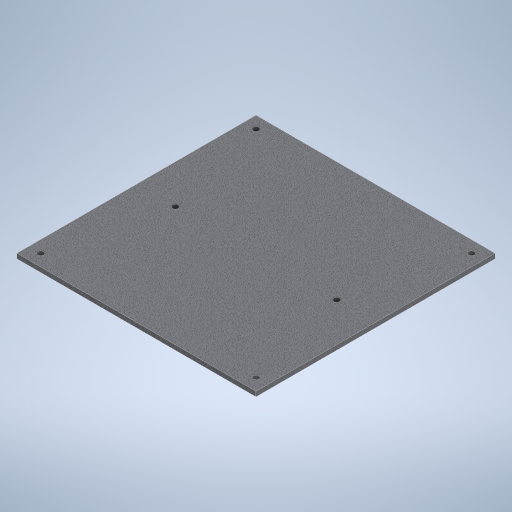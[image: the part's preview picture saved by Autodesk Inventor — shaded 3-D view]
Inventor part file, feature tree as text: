
AUTODESK INVENTOR PART (.ipt)
format: ipt  version: 2023 (Build 270158000, 158)  size: 349,184 bytes
history: native  units: mm
features: sketch x3, hole x2, other x1, extrude x1
ambient origin geometry x8: Origin, YZ Plane, XZ Plane, XY Plane, X Axis, Y Axis, Z Axis, Center Point
bodies: Body1 (feature_tree)
feature tree (7):
  other  "Sólido1"
  extrude  "Extrusão1"  Depth=200.0mm
  hole  "Furo1"  [1 undecoded]
  hole  "Furo2"  [1 undecoded]
  sketch  "Esboço1"  dims[d0=200.0mm d1=200.0mm]
  sketch  "Esboço2"  dims[d2=4.0mm d3=0.0mm d4=10.0mm]
  sketch  "Esboço3"  dims[d5=10.0mm d6=10.0mm d7=10.0mm d8=10.0mm d9=10.0mm d10=10.0mm d11=10.0mm d12=5.0mm d13=6.0mm d14=4.0mm d15=2.0mm d16=90.0deg d17=0.5mm d18=20.594885mm d22=135.0mm d27=5.0mm d28=6.0mm d29=4.0mm d30=2.0mm d31=90.0deg d32=0.5mm d33=20.594885mm d34=200.0mm d35=200.0mm d46=200.0mm d49=100.0mm d50=0.0mm d51=32.5mm]
note: 2 required parameter values undecoded (feature->parameter linkage not recoverable at this tier; creation-order binding heuristic only, values carry confidence <= 0.55)
